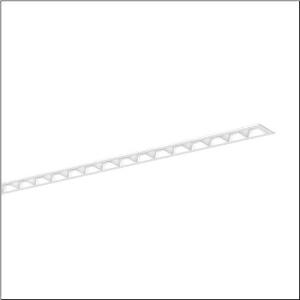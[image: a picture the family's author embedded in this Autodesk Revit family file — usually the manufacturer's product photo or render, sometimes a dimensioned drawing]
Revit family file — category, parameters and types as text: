
# Revit family: silica_r__21_51mx16dc3awb_c0f3
name_source: partatom
category: Lighting Fixtures
units: mm (PartAtom-declared; Revit-internal decimal feet)

## family parameters
Cut with Voids When Loaded = No
Host = Face
Light Source = No
Part Type = Normal
Room Calculation Point = No
Round Connector Dimension = Use Diameter
Shared = No

## types (1)
- --- (1 x LED, 10800 lm, 63.6 W, 3000K)
    Apparent Load = 64 VA
    CIE Flux Codes = 83 98 100 100 100
    Color Rendering = 80
    Color Temperature = 3000K
    Default Elevation = 1800 mm
    Description = Silica® 21, office luminaire, primary light control with darklight reflector, of PMMA, white, CAT 2 (L<= 3000cd/m²), light emission: direct distribution, primary light characteristic: symmetric, installation type: recessed, LED, rated luminous flux: 10.800lm, luminous efficacy: 170lm/W, light colour: 830, colour temperature: 3000K, with terminal, 3+2-pole, max. 2.5mm², mains connection: 220..240V, AC, 50/60Hz, rated input power: 63.6W, luminaire housing, of aluminium, traffic white (RAL 9016), length: 3.028mm, width: 79mm, height: 53mm, protection rating (complete): IP20, insulation class (complete): insulation class I (protective earthing), certification: CE, permissible operating ambient temperature: 0..+35°C, standard: EN 50419, packaging unit: 1 piece
    Height = 0 mm  [stored 0 ft]
    Lamp = 1 x LED
    Lamp Light Flux = 10800 lm
    Lamp Power = 63.6 W
    Lamp count = 1
    Length = 3027 mm
    Luminous efficacy = 170 lm/W
    Manufacturer = Siteco
    ModVariant = No
    Model = 51MX16DC3AWB
    Mounting Place = Ceiling
    Mounting Type = Recessed
    Number of Poles = 1
    OnlyDefault = Yes
    Power Factor = 1
    Product Name = Silica® 21
    Product group = office luminaire | ceiling recessed
    ProductGroupID = 401
    Protection Class = Protection class I
    Protection Degree = IP 20
    RLX_Detail_Level = 1
    RLX_Emergency_Light_Flux = 0 lm
    RLX_Emergency_Type = 0
    RLX_Emergency_Type_DB = No
    RlxData = <blob elided: 60045 chars, md5=ea430760>
    Socket = socket
    Standby Power = 0 W
    System Light Flux = 10800 lm
    System Power = 64 W
    Type Comments = factory setting: luminous flux: 100 % | dim-lin: 254 | 360 mA
    Type Image = l_1297786.jpg
    URL = http://relux.com
    VarID = @adj_055031
    Voltage = 0 V
    Weight = 0.00 kg
    Width = 79 mm

note: [stored X ft] marks values corroborated as IEEE doubles in the binary element streams (Revit-internal decimal feet)

## geometry (parser evidence)
native form markers: Blend x4, Sweep x10
no freeform markers — native parametric forms only
